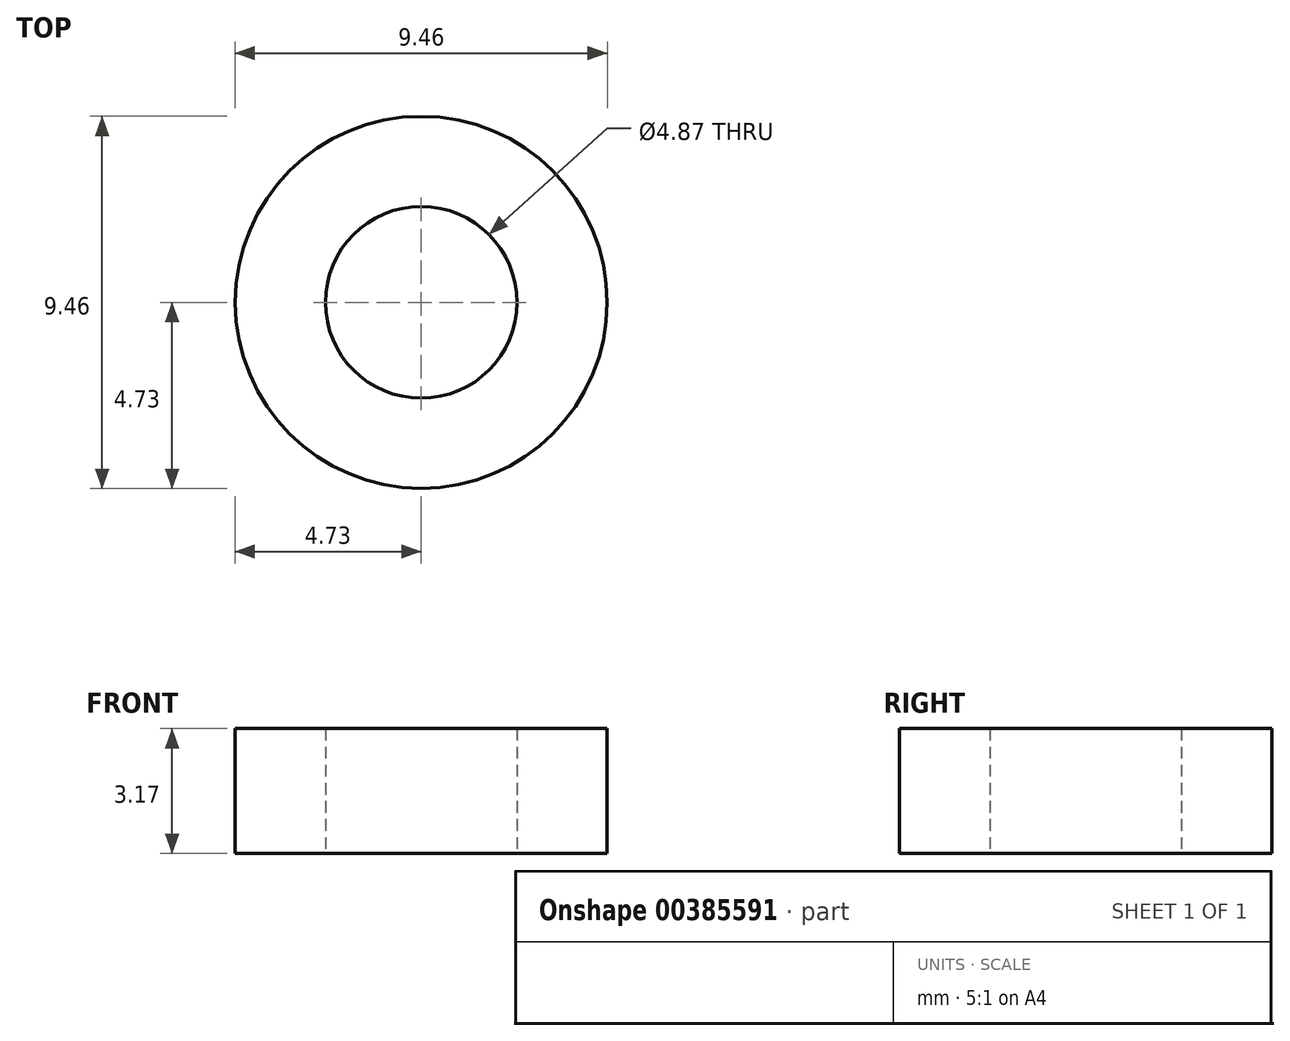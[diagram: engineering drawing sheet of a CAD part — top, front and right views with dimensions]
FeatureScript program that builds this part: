
annotation { "Feature Type Name" : "Feature", "Feature Type Description" : "" }
export const myFeature = defineFeature(function(context is Context, id is Id, definition is map)
    precondition{}
    {
        {
            var Q0;
            Q0=qCreatedBy(makeId("Top.planeOp"),FACE);
            var sketch = newSketch(context, id + "F0", { "sketchPlane" : qUnion([Q0])});
            skCircle(sketch, "E0", {"center": v(0, 0) * mm, "radius": 4.72 * mm});
            skCircle(sketch, "E1", {"center": v(0, 0) * mm, "radius": 2.44 * mm});
            skSolve(sketch);
        }
        {
            var Q0;
            Q0=makeQuery(id+"F0.imprint","IMPRINT",FACE,{"disambiguationData":[TD([[makeQuery(id+"F0.imprint","IMPRINT",EDGE,{"derivedFrom":sQuery(id+"F0.wireOp",EDGE,"E0")}),1.0]])]});
            extrude(context, id + "F1", {"entities" : qUnion([Q0]), "depth" : 3.17 * mm});
        }
    });
